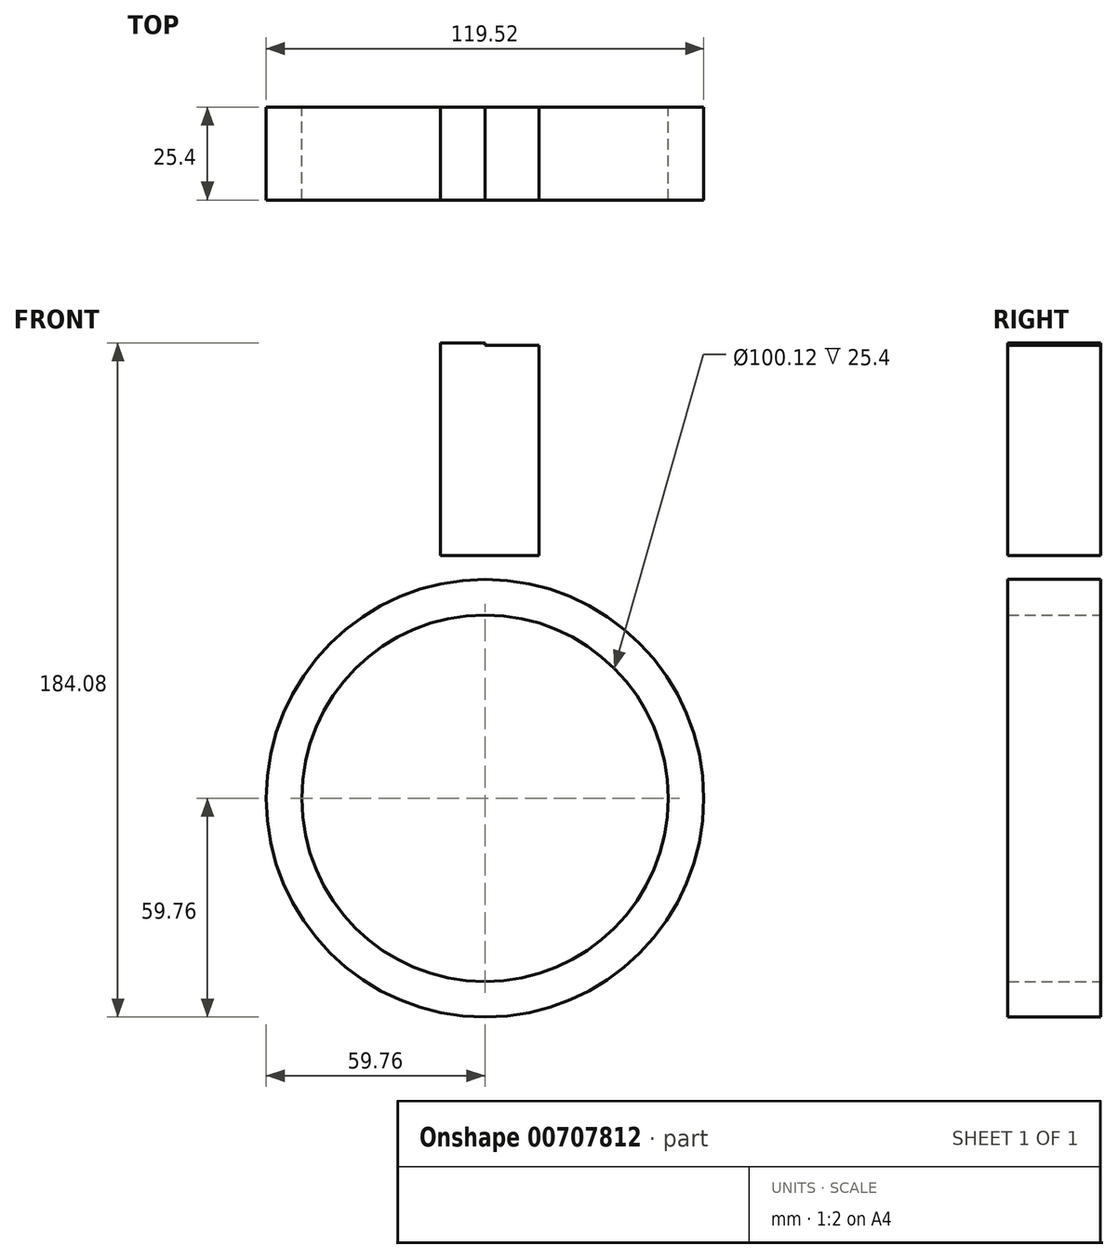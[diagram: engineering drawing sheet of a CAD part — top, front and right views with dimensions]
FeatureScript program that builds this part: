
annotation { "Feature Type Name" : "Feature", "Feature Type Description" : "" }
export const myFeature = defineFeature(function(context is Context, id is Id, definition is map)
    precondition{}
    {
        {
            var Q0;
            Q0=qCreatedBy(makeId("Front.planeOp"),FACE);
            var sketch = newSketch(context, id + "F0", { "sketchPlane" : qUnion([Q0])});
            skCircle(sketch, "E0", {"center": v(0, 0) * mm, "radius": 59.76 * mm});
            skCircle(sketch, "E1", {"center": v(0, 0) * mm, "radius": 50.06 * mm});
            skSolve(sketch);
        }
        {
            var Q0;
            Q0 = qSketchRegion(id + "F0", true);
            var sketch = newSketch(context, id + "F1", { "sketchPlane" : qUnion([Q0])});
            skSolve(sketch);
        }
        {
            var Q0;
            Q0=makeQuery(id+"F1.imprint","IMPRINT",FACE,{"disambiguationData":[TD([[makeQuery(id+"F1.imprint","IMPRINT",EDGE,{"derivedFrom":makeQuery(id+"F0.imprint","IMPRINT",EDGE,{"derivedFrom":sQuery(id+"F0.wireOp",EDGE,"E0")})}),1.0]])]});
            extrude(context, id + "F2", {"entities" : qUnion([Q0]), "depth" : 25.4 * mm, "offsetDistance" : 25.4 * mm});
        }
        {
            var Q0;
            Q0=qCreatedBy(makeId("Front.planeOp"),FACE);
            var sketch = newSketch(context, id + "F3", { "sketchPlane" : qUnion([Q0])});
            skLineSegment(sketch, "E2.bottom", {"start": v(0, 66.29) * mm, "end": v(14.82, 66.29) * mm});
            skLineSegment(sketch, "E2.top", {"start": v(0, 123.72) * mm, "end": v(14.82, 123.72) * mm});
            skLineSegment(sketch, "E2.left", {"start": v(0, 66.29) * mm, "end": v(0, 123.72) * mm});
            skLineSegment(sketch, "E2.right", {"start": v(14.82, 66.29) * mm, "end": v(14.82, 123.72) * mm});
            skLineSegment(sketch, "E3.bottom", {"start": v(0, 66.29) * mm, "end": v(-12.2, 66.29) * mm});
            skLineSegment(sketch, "E3.top", {"start": v(0, 124.32) * mm, "end": v(-12.2, 124.32) * mm});
            skLineSegment(sketch, "E3.left", {"start": v(0, 66.29) * mm, "end": v(0, 124.32) * mm});
            skLineSegment(sketch, "E3.right", {"start": v(-12.2, 66.29) * mm, "end": v(-12.2, 124.32) * mm});
            skSolve(sketch);
        }
        {
            var Q0;
            Q0 = qSketchRegion(id + "F3", true);
            extrude(context, id + "F4", {"entities" : qUnion([Q0]), "depth" : 25.4 * mm, "offsetDistance" : 25.4 * mm});
        }
    });
